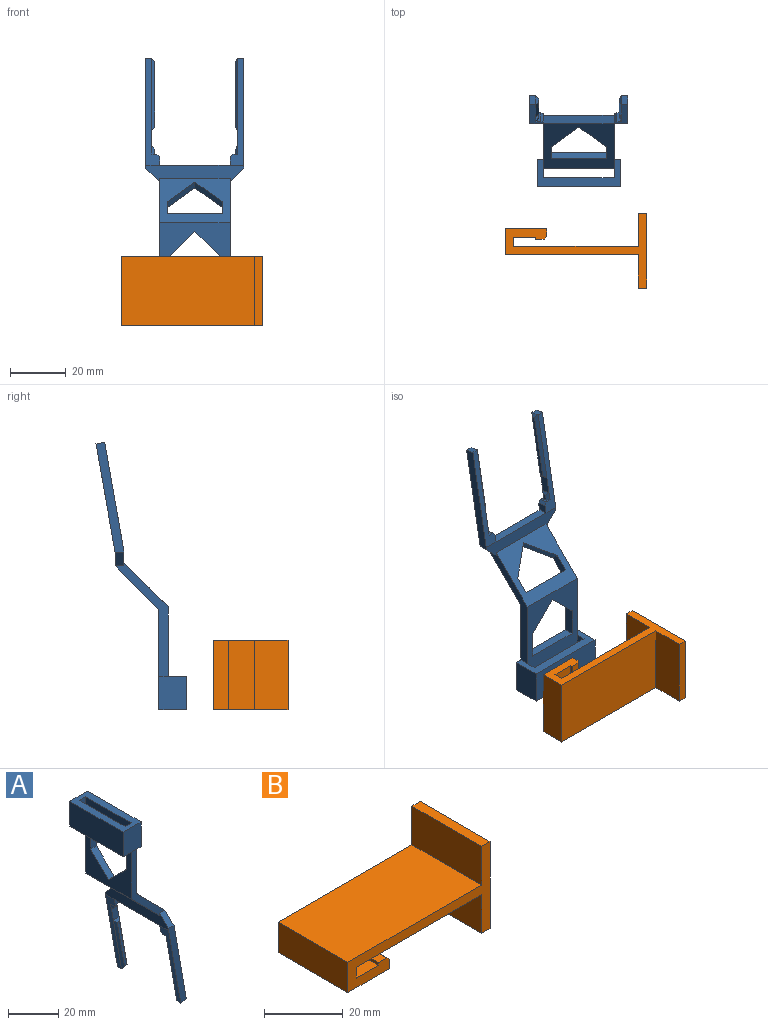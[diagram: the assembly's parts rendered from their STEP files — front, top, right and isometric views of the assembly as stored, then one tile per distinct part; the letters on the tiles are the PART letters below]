
ASSEMBLY  parts=2 mates=1
PART A: 63 faces, bbox 32.6x35.4x96.3 mm
  f0: plane 25.4x15.7mm, normal (0.71,0,0.71), area 344mm2, adj f3,f15,f24,f25,f58,f59,f60,f61
  f1: plane 25.4x16mm, normal (-0.71,0,-0.71), area 354.7mm2, adj f2,f15,f24,f26,f58,f59,f60,f61
  f2: plane 37x25.4mm, normal (-1,0,0), area 639.8mm2, adj f1,f15,f20,f21,f22,f24,f53,f54
  f3: plane 36.06x30mm, normal (1,0,0), area 671.1mm2, adj f0,f15,f16,f18,f22,f23,f24,f53
  f4: plane 25.61x5.33mm, normal (-0.7,0.71,-0.12), area 35.4mm2, adj f6,f28,f45,f52
  f5: plane 25.61x5.33mm, normal (0.7,0.71,0.12), area 35.4mm2, adj f6,f30,f45,f52
  f6: plane 23.84x5.35mm, normal (0,1,0), area 28.8mm2, adj f4,f5,f45,f52
  f7: plane 3.13x1.33mm, normal (-0.7,-0.71,-0.12), area 3.5mm2, adj f8,f11,f35,f48
  f8: plane 2.18x1.53mm, normal (0,-1,0), area 2.4mm2, adj f7,f9,f35,f48
  f9: plane 2.95x1.51mm, normal (0.7,-0.71,0.12), area 3.5mm2, adj f8,f10,f35,f48
  f10: plane 39.39x6.95mm, normal (0.98,0,0.17), area 101.4mm2, adj f9,f13,f14,f25,f32,f33,f35,f38
  f11: plane 38.53x6.79mm, normal (-0.98,0,-0.17), area 97.1mm2, adj f7,f13,f14,f26,f32,f35,f36,f43
  f12: plane 4.5x3.69mm, normal (0,1,0), area 9.3mm2, adj f25,f27,f28,f30,f51
  f13: plane 3.15x2.2mm, normal (0.17,0,-0.98), area 7mm2, adj f10,f11,f32,f46
  f14: plane 4.5x3.69mm, normal (0,-1,0), area 9.3mm2, adj f10,f11,f25,f27,f49
  f15: plane 41x19mm, normal (0,1,0), area 146.3mm2, adj f0,f1,f2,f3,f23,f26,f33
  f16: plane 12x10mm, normal (0,1,0), area 120mm2, adj f3,f17,f22,f23
  f17: plane 30x12mm, normal (-1,0,0), area 360mm2, adj f16,f18,f22,f23
  f18: plane 12x10mm, normal (0,-1,0), area 120mm2, adj f3,f17,f22,f23
  f19: plane 25.4x12mm, normal (1,0,0), area 304.8mm2, adj f20,f21,f22,f23
  f20: plane 12x3.4mm, normal (0,-1,0), area 40.8mm2, adj f2,f19,f22,f23
  f21: plane 12x3.4mm, normal (0,1,0), area 40.8mm2, adj f2,f19,f22,f23
  f22: plane 30x10mm, normal (0,0,1), area 213.6mm2, adj f2,f3,f16,f17,f18,f19,f20,f21
  f23: plane 30x10mm, normal (0,0,-1), area 129.8mm2, adj f3,f15,f16,f17,f18,f19,f20,f21
  f24: plane 41x19mm, normal (0,-1,0), area 146.3mm2, adj f0,f1,f2,f3,f23,f26,f34
  f25: plane 34.57x6mm, normal (1,0,0), area 173.4mm2, adj f0,f10,f12,f14,f27,f30,f33,f34
  f26: plane 35.4x6mm, normal (-1,0,0), area 155.8mm2, adj f1,f11,f15,f24,f27,f28,f31,f32
  f27: plane 25.4x3mm, normal (0,0,-1), area 76.2mm2, adj f12,f14,f25,f26
  f28: plane 38.53x6.79mm, normal (-0.98,0,-0.17), area 97.1mm2, adj f4,f12,f26,f29,f31,f39,f40,f44
  f29: plane 3.15x2.2mm, normal (0.17,0,-0.98), area 7mm2, adj f28,f30,f31,f45
  f30: plane 39.39x6.95mm, normal (0.98,0,0.17), area 101.4mm2, adj f5,f12,f25,f29,f31,f34,f39,f41
  f31: plane 39.53x9.95mm, normal (0,-1,0), area 127.5mm2, adj f26,f28,f29,f30,f34
  f32: plane 39.53x9.95mm, normal (0,1,0), area 127.5mm2, adj f10,f11,f13,f26,f33
  f33: plane 5x5mm, normal (0,0.71,0.71), area 21.2mm2, adj f10,f15,f25,f26,f32
  f34: plane 5x5mm, normal (0,-0.71,0.71), area 21.2mm2, adj f24,f25,f26,f30,f31
  f35: plane 3.15x1.8mm, normal (0.17,0,-0.98), area 3.6mm2, adj f7,f8,f9,f10,f11,f49
  f36: plane 25.61x5.33mm, normal (-0.7,-0.71,-0.12), area 35.4mm2, adj f11,f37,f46,f47
  f37: plane 23.84x5.35mm, normal (0,-1,0), area 28.8mm2, adj f36,f38,f46,f47
  f38: plane 25.61x5.33mm, normal (0.7,-0.71,0.12), area 35.4mm2, adj f10,f37,f46,f47
  f39: plane 3.15x1.8mm, normal (0.17,0,-0.98), area 3.6mm2, adj f28,f30,f40,f41,f42,f51
  f40: plane 3.13x1.33mm, normal (-0.7,0.71,-0.12), area 3.5mm2, adj f28,f39,f42,f50
  f41: plane 2.95x1.51mm, normal (0.7,0.71,0.12), area 3.5mm2, adj f30,f39,f42,f50
  f42: plane 2.18x1.53mm, normal (0,1,0), area 2.4mm2, adj f39,f40,f41,f50
  f43: plane 6.46x4.19mm, normal (0,-1,0), area 19.2mm2, adj f10,f11,f47,f48
  f44: plane 6.46x4.19mm, normal (0,1,0), area 19.2mm2, adj f28,f30,f50,f52
  f45: plane 3.15x1.37mm, normal (0.12,0.71,-0.7), area 3.1mm2, adj f4,f5,f6,f29
  f46: plane 3.15x1.37mm, normal (0.12,-0.71,-0.7), area 3.1mm2, adj f13,f36,f37,f38
  f47: plane 3.15x1.37mm, normal (-0.12,-0.71,0.7), area 3.1mm2, adj f36,f37,f38,f43
  f48: plane 3.15x1.37mm, normal (0.12,-0.71,-0.7), area 3.1mm2, adj f7,f8,f9,f43
  f49: plane 3.33x1.54mm, normal (0.12,-0.71,-0.7), area 4.5mm2, adj f10,f11,f14,f35
  f50: plane 3.15x1.37mm, normal (0.12,0.71,-0.7), area 3.1mm2, adj f40,f41,f42,f44
  f51: plane 3.33x1.54mm, normal (0.12,0.71,-0.7), area 4.5mm2, adj f12,f28,f30,f39
  f52: plane 3.15x1.37mm, normal (-0.12,0.71,0.7), area 3.1mm2, adj f4,f5,f6,f44
  f53: plane 20x3.3mm, normal (0,0,-1), area 66mm2, adj f2,f3,f54,f55
  f54: plane 10x3.3mm, normal (0,1,0), area 33mm2, adj f2,f3,f53,f56
  f55: plane 10x3.3mm, normal (0,-1,0), area 33mm2, adj f2,f3,f53,f57
  f56: plane 10x10mm, normal (0,0.71,0.71), area 46.7mm2, adj f2,f3,f54,f57
  f57: plane 10x10mm, normal (0,-0.71,0.71), area 46.7mm2, adj f2,f3,f55,f56
  f58: plane 20x2.12mm, normal (0.71,0,-0.71), area 60mm2, adj f0,f1,f59,f60
  f59: plane 6.36x6.36mm, normal (0,1,0), area 18mm2, adj f0,f1,f58,f62
  f60: plane 6.36x6.36mm, normal (0,-1,0), area 18mm2, adj f0,f1,f58,f61
  f61: plane 10x9.19mm, normal (-0.5,-0.71,0.5), area 42.4mm2, adj f0,f1,f60,f62
  f62: plane 10x9.19mm, normal (-0.5,0.71,0.5), area 42.4mm2, adj f0,f1,f59,f61
PART B: 17 faces, bbox 51x25x27 mm
  f0: plane 25x12mm, normal (-1,0,0), area 300mm2, adj f1,f13,f14,f15
  f1: plane 48x25mm, normal (0,0,1), area 1200mm2, adj f0,f2,f14,f15
  f2: plane 25x9.4mm, normal (-1,0,0), area 235mm2, adj f1,f3,f14,f15
  f3: plane 25x15mm, normal (0,0,-1), area 375mm2, adj f2,f4,f14,f15
  f4: plane 25x2.8mm, normal (1,0,0), area 70mm2, adj f3,f14,f15,f16
  f5: plane 25x3mm, normal (0,0,1), area 75mm2, adj f6,f14,f15,f16
  f6: plane 25x0.8mm, normal (-1,0,0), area 20mm2, adj f5,f7,f14,f15
  f7: plane 25x8mm, normal (0,0,1), area 200mm2, adj f6,f8,f14,f15
  f8: plane 25x3.4mm, normal (1,0,0), area 85mm2, adj f7,f9,f14,f15
  f9: plane 45x25mm, normal (0,0,-1), area 1125mm2, adj f8,f10,f14,f15
  f10: plane 25x12mm, normal (-1,0,0), area 300mm2, adj f9,f11,f14,f15
  f11: plane 25x3mm, normal (0,0,-1), area 75mm2, adj f10,f12,f14,f15
  f12: plane 27x25mm, normal (1,0,0), area 675mm2, adj f11,f13,f14,f15
  f13: plane 25x3mm, normal (0,0,1), area 75mm2, adj f0,f12,f14,f15
  f14: plane 51x27mm, normal (0,-1,0), area 282.9mm2, adj f0,f1,f2,f3,f4,f5,f6,f7
  f15: plane 51x27mm, normal (0,1,0), area 282.9mm2, adj f0,f1,f2,f3,f4,f5,f6,f7
  f16: plane 25x1mm, normal (0.71,0,0.71), area 35.4mm2, adj f4,f5,f14,f15
PLACE A rot(axis=(-0.71,-0.71,0),180deg) t=(12.96,15.59,9.73)mm
PLACE B rot(axis=(1,0,0),90deg) t=(21.95,-12.4,22.73)mm
MATE planar A.f22 <-> B.f14  axis (0,0,-1) through (0.46,12.09,-2.27)mm
